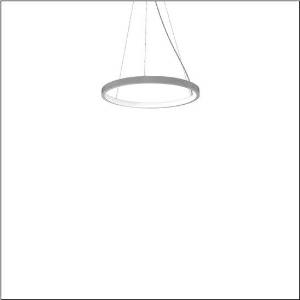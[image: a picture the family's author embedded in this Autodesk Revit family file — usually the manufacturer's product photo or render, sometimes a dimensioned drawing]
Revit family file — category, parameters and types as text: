
# Revit family: silica_r__21_ring-i_5pjbi1d3204a_3771
name_source: partatom
category: Lighting Fixtures
units: mm (PartAtom-declared; Revit-internal decimal feet)

## family parameters
Cut with Voids When Loaded = No
Host = Face
Light Source = No
Part Type = Normal
Room Calculation Point = No
Round Connector Dimension = Use Diameter
Shared = No

## types (1)
- Silica® 21 Ring-I (1 x LED, 3510 lm, 60 W, 4000K)
    Apparent Load = 60 VA
    CIE Flux Codes = 22 48 76 50 101
    Color Rendering = 80
    Color Temperature = 4000K
    Default Elevation = 1800 mm
    Description = Silica® 21 Ring-I, suspended luminaire, of PMMA, frosted, light emission: inner ring side luminous distribution, primary light characteristic: symmetric, installation type: suspended mounting, LED, rated luminous flux: 3.510lm, luminous efficacy: 59lm/W, light colour: 840, colour temperature: 4000K, control gear: DALI 2, with terminal, 5-pole, mains connection: 230V, AC/DC, 0/50..60Hz, rated input power: 60W, housing, of extruded aluminium section, metallic grey (RAL 9006), diameter: 610mm, ceiling canopy, metallic grey (RAL 9006), protection rating (lamp compartment): IP40, insulation class (complete): insulation class I (protective earthing), certification: CE, impact resistance: IK02, permissible operating ambient temperature: 0..+35°C, packaging unit: 1 piece
    Height = 48 mm  [stored 0.15748 ft]
    Lamp = 1 x LED
    Lamp Light Flux = 3510 lm
    Lamp Power = 60 W
    Lamp count = 1
    Length = 610 mm
    Luminous efficacy = 59 lm/W
    Manufacturer = Siteco
    ModVariant = No
    Model = 5PJBI1D3204A
    Mounting Place = Ceiling
    Mounting Type = Pendant
    Number of Poles = 1
    OnlyDefault = Yes
    Power Factor = 1
    Product Name = Silica® 21 Ring-I
    Product group = suspended luminaire
    ProductGroupID = 905
    Protection Class = Protection class I
    Protection Degree = IP 40
    RLX_Detail_Level = 1
    RLX_Emergency_Light_Flux = 0 lm
    RLX_Emergency_Type = 0
    RLX_Emergency_Type_DB = No
    RlxData = <blob elided: 11513 chars, md5=bc1aae0f>
    Socket = socket
    Standby Power = 0 W
    System Light Flux = 3510 lm
    System Power = 60 W
    Type Comments = Product without accessories
    Type Image = l_1251750.jpg
    URL = http://relux.com
    VarID = ---
    Voltage = 0 V
    Weight = 0.00 kg
    Width = 0 mm  [stored 0 ft]

note: [stored X ft] marks values corroborated as IEEE doubles in the binary element streams (Revit-internal decimal feet)

## geometry (parser evidence)
native form markers: Sweep x12
no freeform markers — native parametric forms only
